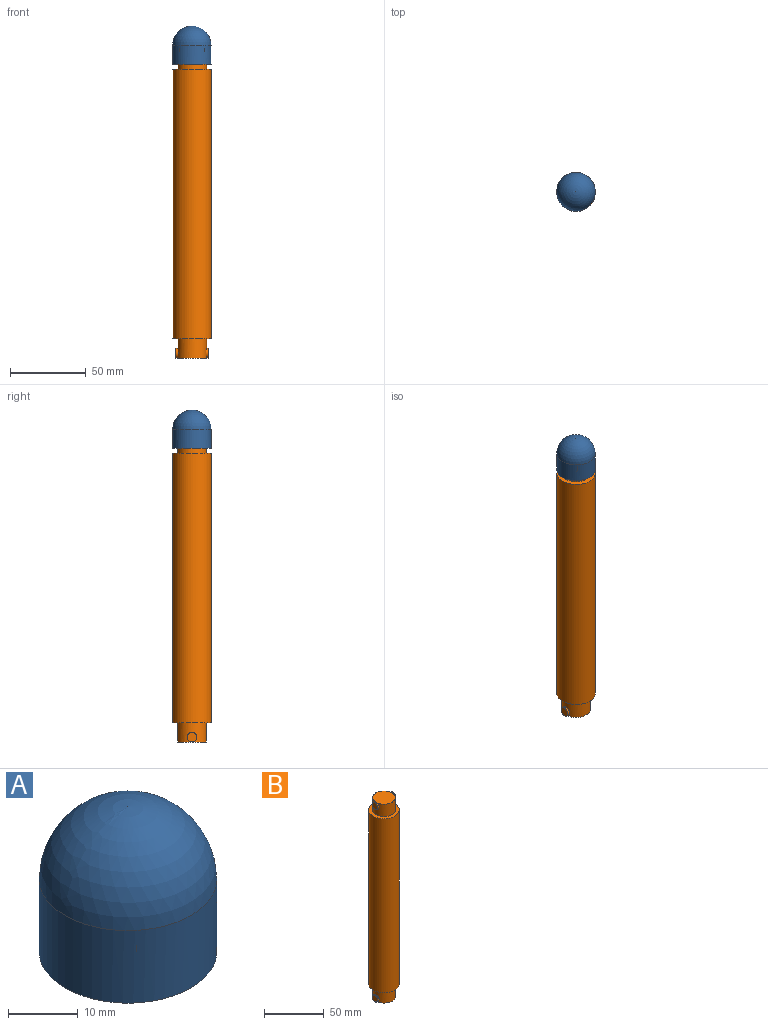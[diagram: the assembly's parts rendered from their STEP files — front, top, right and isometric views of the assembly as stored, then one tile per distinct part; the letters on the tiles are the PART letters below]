
ASSEMBLY  parts=2 mates=1
PART A: 28 faces, bbox 25.4x25.4x25.4 mm
  f0: cylinder r=9.65mm len=13.96mm, axis (0,0,-1), area 112.5mm2, adj f4,f11,f24,f25
  f1: cylinder r=9.65mm len=14.31mm, axis (0,0,-1), area 17.4mm2, adj f7,f11
  f2: cylinder r=9.65mm len=13.96mm, axis (0,0,-1), area 112.5mm2, adj f4,f10,f26,f27
  f3: cylinder r=12.7mm len=25.4mm, axis (0,0,-1), area 1013.4mm2, adj f4,f5
  f4: plane 25.4x25.4mm, normal (0,0,-1), area 186.3mm2, adj f0,f2,f3,f8,f9,f24,f25,f26
  f5: sphere r=12.7mm, area 1013.4mm2, adj f3
  f6: cylinder r=9.65mm len=14.31mm, axis (0,0,-1), area 17.4mm2, adj f7,f10
  f7: plane 21.84x19.3mm, normal (0,0,-1), area 326.2mm2, adj f1,f6,f8,f9,f10,f11,f12,f15
  f8: plane 12.7x6.6mm, normal (1,0,0), area 83.9mm2, adj f4,f7,f25,f27
  f9: plane 12.7x6.6mm, normal (-1,0,0), area 83.9mm2, adj f4,f7,f24,f26
  f10: cylinder r=3.3mm len=17.78mm, axis (1,0,0), area 97.5mm2, adj f2,f6,f7,f13,f14,f20,f21,f26
  f11: cylinder r=3.3mm len=17.78mm, axis (1,0,0), area 97.5mm2, adj f0,f1,f7,f17,f18,f22,f23,f24
  f12: plane 6.6x1.62mm, normal (-1,0,0), area 10.7mm2, adj f7,f13,f20,f26
  f13: plane 1.73x1.62mm, normal (0,0,1), area 1.4mm2, adj f10,f12,f26
  f14: plane 1.73x1.62mm, normal (0,0,1), area 1.4mm2, adj f10,f15,f27
  f15: plane 6.6x1.62mm, normal (1,0,0), area 10.7mm2, adj f7,f14,f21,f27
  f16: plane 6.6x1.62mm, normal (-1,0,0), area 10.7mm2, adj f7,f17,f22,f24
  f17: plane 1.73x1.62mm, normal (0,0,1), area 1.4mm2, adj f11,f16,f24
  f18: plane 1.73x1.62mm, normal (0,0,1), area 1.4mm2, adj f11,f19,f25
  f19: plane 6.6x1.62mm, normal (1,0,0), area 10.7mm2, adj f7,f18,f23,f25
  f20: cylinder r=25.4mm len=6.6mm, axis (0,0,1), area 17.7mm2, adj f10,f12
  f21: cylinder r=25.4mm len=6.6mm, axis (0,0,1), area 17.7mm2, adj f10,f15
  f22: cylinder r=25.4mm len=6.6mm, axis (0,0,1), area 17.7mm2, adj f11,f16
  f23: cylinder r=25.4mm len=6.6mm, axis (0,0,1), area 17.7mm2, adj f11,f19
  f24: cylinder r=25.4mm len=12.7mm, axis (0,0,-1), area 48.6mm2, adj f0,f4,f7,f9,f11,f16,f17
  f25: cylinder r=25.4mm len=12.7mm, axis (0,0,1), area 48.6mm2, adj f0,f4,f7,f8,f11,f18,f19
  f26: cylinder r=25.4mm len=12.7mm, axis (0,0,-1), area 48.6mm2, adj f2,f4,f7,f9,f10,f12,f13
  f27: cylinder r=25.4mm len=12.7mm, axis (0,0,1), area 48.6mm2, adj f2,f4,f7,f8,f10,f14,f15
PART B: 15 faces, bbox 25.4x25.4x203.2 mm
  f0: cylinder r=9.53mm len=19.05mm, axis (0,0,-1), area 695.8mm2, adj f4,f5,f12,f13
  f1: cylinder r=9.53mm len=19.05mm, axis (0,0,-1), area 695.9mm2, adj f3,f6,f8,f9
  f2: cylinder r=12.7mm len=177.8mm, axis (0,0,-1), area 14187.8mm2, adj f3,f4
  f3: plane 25.4x25.4mm, normal (0,0,1), area 221.7mm2, adj f1,f2
  f4: plane 25.4x25.4mm, normal (0,0,-1), area 221.7mm2, adj f0,f2
  f5: plane 19.05x19.05mm, normal (0,0,-1), area 285mm2, adj f0
  f6: plane 19.05x19.05mm, normal (0,0,1), area 285mm2, adj f1
  f7: plane 6.35x6.35mm, normal (1,0,0), area 31.7mm2, adj f8
  f8: cylinder r=3.17mm len=6.35mm, axis (-1,0,0), area 30.7mm2, adj f1,f7
  f9: cylinder r=3.17mm len=6.35mm, axis (-1,0,0), area 30.7mm2, adj f1,f10
  f10: plane 6.35x6.35mm, normal (-1,0,0), area 31.7mm2, adj f9
  f11: plane 6.35x6.35mm, normal (1,0,0), area 31.7mm2, adj f12
  f12: cylinder r=3.17mm len=6.35mm, axis (-1,0,0), area 30.7mm2, adj f0,f11
  f13: cylinder r=3.17mm len=6.35mm, axis (-1,0,0), area 30.7mm2, adj f0,f14
  f14: plane 6.35x6.35mm, normal (-1,0,0), area 31.7mm2, adj f13
PLACE A t=(-84.9,-54.95,79.58)mm
PLACE B t=(-84.77,-54.95,-12.49)mm
MATE fastened B.f8 <-> A.f9  axis (1,0,0) through (-73.97,-54.95,85.93)mm
